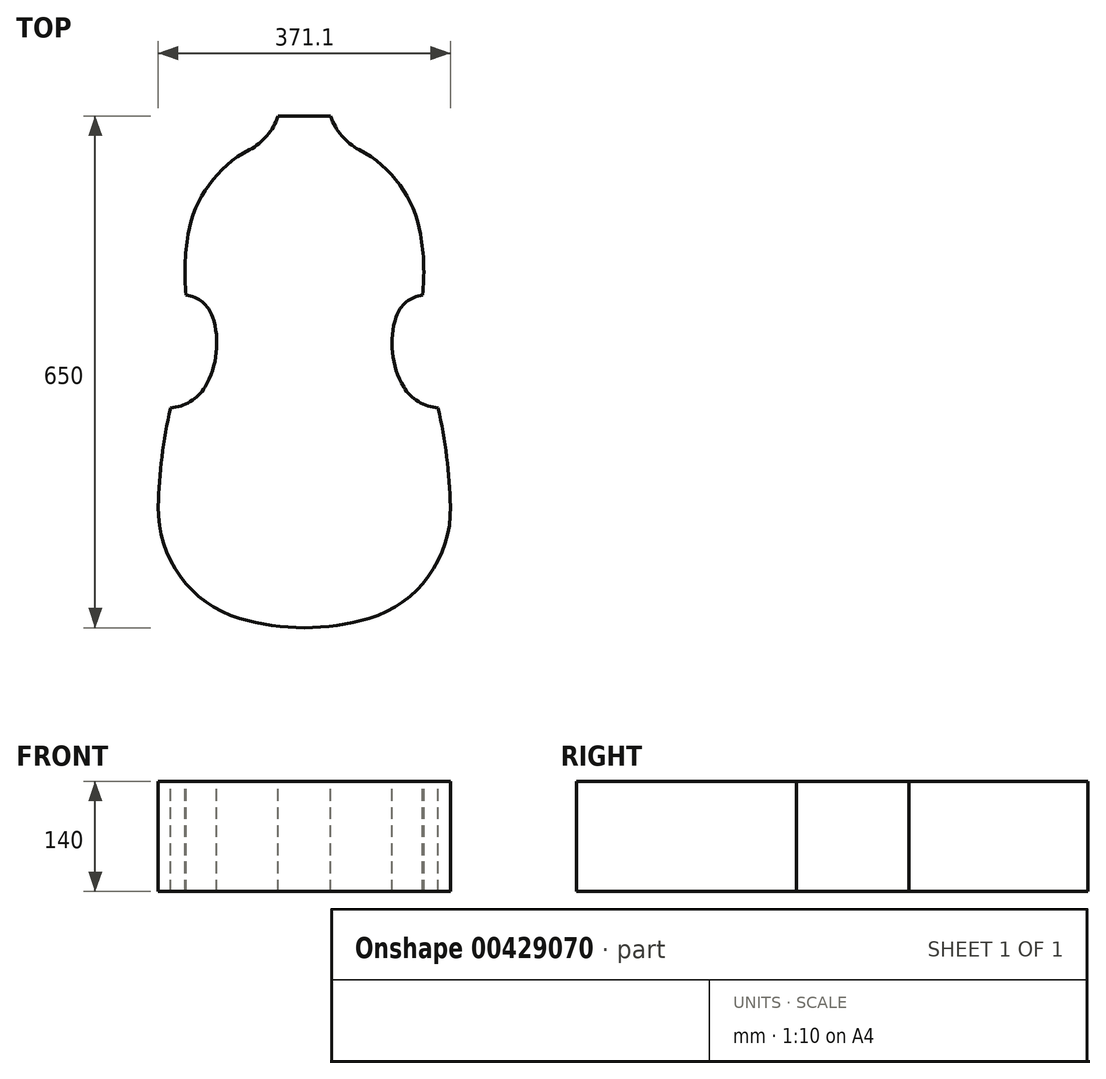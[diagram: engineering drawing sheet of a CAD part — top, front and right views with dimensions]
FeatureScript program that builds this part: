
annotation { "Feature Type Name" : "Feature", "Feature Type Description" : "" }
export const myFeature = defineFeature(function(context is Context, id is Id, definition is map)
    precondition{}
    {
        {
            var Q0;
            Q0=qCreatedBy(makeId("Top.planeOp"),FACE);
            var sketch = newSketch(context, id + "F0", { "sketchPlane" : qUnion([Q0])});
            skLineSegment(sketch, "E0", {"start": v(0, 0) * mm, "end": v(0, 680) * mm, "construction": true});
            skSolve(sketch);
        }
        {
            var Q0;
            Q0=qCreatedBy(makeId("Top.planeOp"),FACE);
            var sketch = newSketch(context, id + "F1", { "sketchPlane" : qUnion([Q0])});
            skLineSegment(sketch, "E1", {"start": v(0, 680) * mm, "end": v(0, 340) * mm});
            skLineSegment(sketch, "E2", {"start": v(0, 340) * mm, "end": v(0, 0) * mm});
            skLineSegment(sketch, "E3", {"start": v(0, 0) * mm, "end": v(0, -340) * mm});
            skSolve(sketch);
        }
        {
            var Q0;
            Q0=qCreatedBy(makeId("Top.planeOp"),FACE);
            var sketch = newSketch(context, id + "F2", { "sketchPlane" : qUnion([Q0])});
            skLineSegment(sketch, "E4", {"start": v(0, 0) * mm, "end": v(0, 68) * mm, "construction": true});
            skSolve(sketch);
        }
        {
            var Q0;
            Q0=qCreatedBy(makeId("Top.planeOp"),FACE);
            var sketch = newSketch(context, id + "F3", { "sketchPlane" : qUnion([Q0])});
            skLineSegment(sketch, "E5", {"start": v(0, 0) * mm, "end": v(0, 650) * mm, "construction": true});
            skPoint(sketch, "E6.endSnap0", {"position": v(0, 325) * mm});
            skLineSegment(sketch, "E7", {"start": v(0, 650) * mm, "end": v(377.25, 650) * mm, "construction": true});
            skSolve(sketch);
        }
        {
            var Q0;
            Q0=qCreatedBy(makeId("Top.planeOp"),FACE);
            var sketch = newSketch(context, id + "F4", { "sketchPlane" : qUnion([Q0])});
            skLineSegment(sketch, "E8", {"start": v(0, 650) * mm, "end": v(0, 577.78) * mm, "construction": true});
            skLineSegment(sketch, "E9", {"start": v(0, 577.78) * mm, "end": v(0, 505.56) * mm, "construction": true});
            skLineSegment(sketch, "E10", {"start": v(0, 505.56) * mm, "end": v(0, 433.33) * mm, "construction": true});
            skLineSegment(sketch, "E11", {"start": v(0, 433.33) * mm, "end": v(0, 361.11) * mm, "construction": true});
            skLineSegment(sketch, "E12", {"start": v(0, 361.11) * mm, "end": v(0, 288.89) * mm, "construction": true});
            skLineSegment(sketch, "E13", {"start": v(0, 288.89) * mm, "end": v(0, 216.67) * mm, "construction": true});
            skLineSegment(sketch, "E14", {"start": v(0, 216.67) * mm, "end": v(0, 144.44) * mm, "construction": true});
            skLineSegment(sketch, "E15", {"start": v(0, 144.44) * mm, "end": v(0, 72.22) * mm, "construction": true});
            skLineSegment(sketch, "E16", {"start": v(0, 72.22) * mm, "end": v(0, 0) * mm, "construction": true});
            skLineSegment(sketch, "E17", {"start": v(0, 0) * mm, "end": v(0, -72.22) * mm, "construction": true});
            skLineSegment(sketch, "E18", {"start": v(0, -72.22) * mm, "end": v(0, -144.44) * mm, "construction": true});
            skLineSegment(sketch, "E19", {"start": v(0, -144.44) * mm, "end": v(0, -216.67) * mm, "construction": true});
            skLineSegment(sketch, "E20", {"start": v(0, -216.67) * mm, "end": v(0, -288.89) * mm, "construction": true});
            skLineSegment(sketch, "E21", {"start": v(-33.5, -288.89) * mm, "end": v(33.5, -288.89) * mm, "construction": true});
            skLineSegment(sketch, "E22", {"start": v(-33.5, 361.11) * mm, "end": v(33.5, 361.11) * mm, "construction": true});
            skLineSegment(sketch, "E23", {"start": v(-577.47, 650) * mm, "end": v(577.47, 650) * mm, "construction": true});
            skLineSegment(sketch, "E24", {"start": v(-580.77, 0) * mm, "end": v(580.77, 0) * mm, "construction": true});
            skLineSegment(sketch, "E25", {"start": v(-583.98, 72.22) * mm, "end": v(583.98, 72.22) * mm, "construction": true});
            skSolve(sketch);
        }
        {
            var Q0;
            Q0=qCreatedBy(makeId("Top.planeOp"),FACE);
            var sketch = newSketch(context, id + "F5", { "sketchPlane" : qUnion([Q0])});
            skCircle(sketch, "E26", {"center": v(0, 0) * mm, "radius": 302.86 * mm});
            skCircle(sketch, "E27", {"center": v(262.29, -151.43) * mm, "radius": 462.53 * mm});
            skLineSegment(sketch, "E28", {"start": v(0, 0) * mm, "end": v(0, -302.86) * mm, "construction": true});
            skLineSegment(sketch, "E29", {"start": v(0, -302.86) * mm, "end": v(262.29, -151.43) * mm, "construction": true});
            skLineSegment(sketch, "E30", {"start": v(262.29, -151.43) * mm, "end": v(0, 0) * mm, "construction": true});
            skCircle(sketch, "E31", {"center": v(-48.7, -143.38) * mm, "radius": 151.43 * mm});
            skArc(sketch, "E32", {"start": v(0, -151.43) * mm, "mid": v(-32.38, -147.93) * mm, "end": v(-63.27, -137.58) * mm});
            skSolve(sketch);
        }
        {
            var Q0;
            Q0=qCreatedBy(makeId("Top.planeOp"),FACE);
            var sketch = newSketch(context, id + "F6", { "sketchPlane" : qUnion([Q0])});
            skLineSegment(sketch, "E33", {"start": v(651.57, 0) * mm, "end": v(651.57, 650) * mm, "construction": true});
            skLineSegment(sketch, "E34", {"start": v(651.57, 650) * mm, "end": v(756.75, 650) * mm, "construction": true});
            skLineSegment(sketch, "E35", {"start": v(756.75, 650) * mm, "end": v(756.75, 557.14) * mm, "construction": true});
            skLineSegment(sketch, "E36", {"start": v(756.75, 557.14) * mm, "end": v(756.75, 464.29) * mm, "construction": true});
            skLineSegment(sketch, "E37", {"start": v(756.75, 464.29) * mm, "end": v(756.75, 371.43) * mm, "construction": true});
            skLineSegment(sketch, "E38", {"start": v(756.75, 371.43) * mm, "end": v(756.75, 278.57) * mm, "construction": true});
            skLineSegment(sketch, "E39", {"start": v(756.75, 278.57) * mm, "end": v(756.75, 185.71) * mm, "construction": true});
            skLineSegment(sketch, "E40", {"start": v(756.75, 185.71) * mm, "end": v(756.75, 92.86) * mm, "construction": true});
            skLineSegment(sketch, "E41", {"start": v(756.75, 92.86) * mm, "end": v(756.75, 0) * mm, "construction": true});
            skLineSegment(sketch, "E42", {"start": v(756.75, 0) * mm, "end": v(651.57, 0) * mm, "construction": true});
            skLineSegment(sketch, "E43", {"start": v(-464.29, -151.43) * mm, "end": v(-464.29, 498.57) * mm, "construction": true});
            skLineSegment(sketch, "E44", {"start": v(-464.29, -151.43) * mm, "end": v(-371.43, -151.43) * mm, "construction": true});
            skLineSegment(sketch, "E45", {"start": v(-371.43, -151.43) * mm, "end": v(-278.57, -151.43) * mm, "construction": true});
            skLineSegment(sketch, "E46", {"start": v(-278.57, -151.43) * mm, "end": v(-185.71, -151.43) * mm, "construction": true});
            skLineSegment(sketch, "E47", {"start": v(-185.71, -151.43) * mm, "end": v(-92.86, -151.43) * mm, "construction": true});
            skLineSegment(sketch, "E48", {"start": v(-92.86, -151.43) * mm, "end": v(0, -151.43) * mm, "construction": true});
            skArc(sketch, "E49", {"start": v(-74.73, -279.05) * mm, "mid": v(122.25, -261.75) * mm, "end": v(261.95, -121.8) * mm});
            skArc(sketch, "E50", {"start": v(-464.29, 498.57) * mm, "mid": v(56.93, 236.94) * mm, "end": v(158.56, -337.34) * mm});
            skCircle(sketch, "E51", {"center": v(41.1, -138.47) * mm, "radius": 144.44 * mm});
            skLineSegment(sketch, "E52", {"start": v(41.1, -138.47) * mm, "end": v(41.1, -66.25) * mm, "construction": true});
            skLineSegment(sketch, "E53", {"start": v(41.1, -66.25) * mm, "end": v(41.1, 5.97) * mm, "construction": true});
            skSolve(sketch);
        }
        {
            var Q0;
            Q0=qCreatedBy(makeId("Top.planeOp"),FACE);
            var sketch = newSketch(context, id + "F7", { "sketchPlane" : qUnion([Q0])});
            skLineSegment(sketch, "E54", {"start": v(-464.29, -151.43) * mm, "end": v(-397.96, -88.53) * mm, "construction": true});
            skLineSegment(sketch, "E55", {"start": v(-397.96, -88.53) * mm, "end": v(-331.63, -25.63) * mm, "construction": true});
            skLineSegment(sketch, "E56", {"start": v(-331.63, -25.63) * mm, "end": v(-265.3, 37.28) * mm, "construction": true});
            skLineSegment(sketch, "E57", {"start": v(-265.3, 37.28) * mm, "end": v(-198.98, 100.18) * mm, "construction": true});
            skLineSegment(sketch, "E58", {"start": v(-198.98, 100.18) * mm, "end": v(-132.65, 163.08) * mm, "construction": true});
            skLineSegment(sketch, "E59", {"start": v(-132.65, 163.08) * mm, "end": v(-66.33, 225.99) * mm, "construction": true});
            skLineSegment(sketch, "E60", {"start": v(-66.33, 225.99) * mm, "end": v(0, 288.89) * mm, "construction": true});
            skCircle(sketch, "E61", {"center": v(-132.65, 163.08) * mm, "radius": 284.37 * mm});
            skLineSegment(sketch, "E62", {"start": v(-464.29, 498.57) * mm, "end": v(-464.29, 417.32) * mm, "construction": true});
            skLineSegment(sketch, "E63", {"start": v(-464.29, 417.32) * mm, "end": v(-464.29, 336.07) * mm, "construction": true});
            skLineSegment(sketch, "E64", {"start": v(-464.29, 336.07) * mm, "end": v(-464.29, 254.82) * mm, "construction": true});
            skLineSegment(sketch, "E65", {"start": v(-464.29, 254.82) * mm, "end": v(-464.29, 173.57) * mm, "construction": true});
            skLineSegment(sketch, "E66", {"start": v(-464.29, 173.57) * mm, "end": v(-464.29, 92.32) * mm, "construction": true});
            skLineSegment(sketch, "E67", {"start": v(-464.29, 92.32) * mm, "end": v(-464.29, 11.07) * mm, "construction": true});
            skLineSegment(sketch, "E68", {"start": v(-464.29, 11.07) * mm, "end": v(-464.29, -70.18) * mm, "construction": true});
            skLineSegment(sketch, "E69", {"start": v(-464.29, -70.18) * mm, "end": v(-464.29, -151.43) * mm, "construction": true});
            skCircle(sketch, "E70", {"center": v(-464.29, 132.94) * mm, "radius": 284.37 * mm, "construction": true});
            skPoint(sketch, "E70.centerSnap0", {"position": v(-464.29, 214.2) * mm});
            skLineSegment(sketch, "E71", {"start": v(-180.27, 325) * mm, "end": v(173.93, 325) * mm, "construction": true});
            skCircle(sketch, "E72", {"center": v(0, 185.71) * mm, "radius": 149.8 * mm});
            skCircle(sketch, "E73", {"center": v(104.63, 384.58) * mm, "radius": 74.9 * mm});
            skLineSegment(sketch, "E74", {"start": v(756.75, 185.71) * mm, "end": v(-927.16, 185.71) * mm});
            skLineSegment(sketch, "E75", {"start": v(-132.65, 163.08) * mm, "end": v(0, 185.71) * mm, "construction": true});
            skLineSegment(sketch, "E76", {"start": v(0, 185.71) * mm, "end": v(147.67, 210.9) * mm, "construction": true});
            skLineSegment(sketch, "E77", {"start": v(0, 185.71) * mm, "end": v(34.88, 252) * mm, "construction": true});
            skLineSegment(sketch, "E78", {"start": v(34.88, 252) * mm, "end": v(69.76, 318.29) * mm, "construction": true});
            skLineSegment(sketch, "E79", {"start": v(69.76, 318.29) * mm, "end": v(104.63, 384.58) * mm, "construction": true});
            skSolve(sketch);
        }
        {
            var Q0;
            Q0=qCreatedBy(makeId("Top.planeOp"),FACE);
            var sketch = newSketch(context, id + "F8", { "sketchPlane" : qUnion([Q0])});
            skLineSegment(sketch, "E80", {"start": v(0, 0) * mm, "end": v(0, -57.78) * mm, "construction": true});
            skLineSegment(sketch, "E81", {"start": v(0, -57.78) * mm, "end": v(0, -115.56) * mm, "construction": true});
            skLineSegment(sketch, "E82", {"start": v(0, -115.56) * mm, "end": v(0, -173.33) * mm, "construction": true});
            skLineSegment(sketch, "E83", {"start": v(0, -173.33) * mm, "end": v(0, -231.11) * mm, "construction": true});
            skLineSegment(sketch, "E84", {"start": v(0, -231.11) * mm, "end": v(0, -288.89) * mm, "construction": true});
            skCircle(sketch, "E85", {"center": v(-219.54, 72.22) * mm, "radius": 108.33 * mm});
            skArc(sketch, "E86", {"start": v(0, -231.11) * mm, "mid": v(-187.22, -135.5) * mm, "end": v(-219.54, 72.22) * mm, "construction": true});
            skLineSegment(sketch, "E87", {"start": v(0, 0) * mm, "end": v(0, 108.33) * mm, "construction": true});
            skLineSegment(sketch, "E88", {"start": v(0, 108.33) * mm, "end": v(0, 216.67) * mm, "construction": true});
            skLineSegment(sketch, "E89", {"start": v(0, 216.67) * mm, "end": v(0, 325) * mm, "construction": true});
            skLineSegment(sketch, "E90", {"start": v(0, 325) * mm, "end": v(0, 433.33) * mm, "construction": true});
            skLineSegment(sketch, "E91", {"start": v(0, 433.33) * mm, "end": v(0, 541.67) * mm, "construction": true});
            skLineSegment(sketch, "E92", {"start": v(0, 541.67) * mm, "end": v(0, 650) * mm, "construction": true});
            skLineSegment(sketch, "E93", {"start": v(-219.54, 72.22) * mm, "end": v(-327.87, 72.22) * mm, "construction": true});
            skLineSegment(sketch, "E94", {"start": v(609.32, 650) * mm, "end": v(609.32, 568.75) * mm});
            skLineSegment(sketch, "E95", {"start": v(609.32, 568.75) * mm, "end": v(609.32, 487.5) * mm});
            skLineSegment(sketch, "E96", {"start": v(609.32, 487.5) * mm, "end": v(609.32, 406.25) * mm});
            skLineSegment(sketch, "E97", {"start": v(609.32, 406.25) * mm, "end": v(609.32, 325) * mm});
            skLineSegment(sketch, "E98", {"start": v(609.32, 325) * mm, "end": v(609.32, 243.75) * mm});
            skLineSegment(sketch, "E99", {"start": v(609.32, 243.75) * mm, "end": v(609.32, 162.5) * mm});
            skLineSegment(sketch, "E100", {"start": v(609.32, 162.5) * mm, "end": v(609.32, 81.25) * mm});
            skLineSegment(sketch, "E101", {"start": v(609.32, 81.25) * mm, "end": v(609.32, 0) * mm});
            skCircle(sketch, "E102", {"center": v(609.32, 40.62) * mm, "radius": 40.62 * mm});
            skCircle(sketch, "E103", {"center": v(-172.93, 44.62) * mm, "radius": 54.17 * mm});
            skLineSegment(sketch, "E104", {"start": v(-219.54, 72.22) * mm, "end": v(-155.22, 93.38) * mm, "construction": true});
            skCircle(sketch, "E105", {"center": v(-155.22, 93.38) * mm, "radius": 40.62 * mm});
            skLineSegment(sketch, "E106", {"start": v(-219.54, 72.22) * mm, "end": v(0, -57.78) * mm, "construction": true});
            skLineSegment(sketch, "E107", {"start": v(-155.22, 93.38) * mm, "end": v(0, 144.44) * mm, "construction": true});
            skArc(sketch, "E108", {"start": v(0, -231.11) * mm, "mid": v(187.22, -135.5) * mm, "end": v(219.54, 72.22) * mm, "construction": true});
            skLineSegment(sketch, "E109", {"start": v(0, 144.44) * mm, "end": v(219.54, 72.22) * mm, "construction": true});
            skLineSegment(sketch, "E110", {"start": v(0, -57.78) * mm, "end": v(219.54, 72.22) * mm, "construction": true});
            skCircle(sketch, "E111", {"center": v(219.54, 72.22) * mm, "radius": 108.33 * mm});
            skLineSegment(sketch, "E112", {"start": v(219.54, 72.22) * mm, "end": v(327.87, 72.22) * mm, "construction": true});
            skCircle(sketch, "E113", {"center": v(155.22, 93.38) * mm, "radius": 40.62 * mm});
            skCircle(sketch, "E114", {"center": v(172.93, 44.62) * mm, "radius": 54.17 * mm});
            skSolve(sketch);
        }
        {
            var Q0;
            Q0=qCreatedBy(makeId("Top.planeOp"),FACE);
            var sketch = newSketch(context, id + "F9", { "sketchPlane" : qUnion([Q0])});
            skPoint(sketch, "E115.orphan", {"position": v(-464.29, 498.57) * mm});
            skLineSegment(sketch, "E116", {"start": v(33.5, 361.11) * mm, "end": v(0, 361.11) * mm});
            skLineSegment(sketch, "E117", {"start": v(0, 361.11) * mm, "end": v(0, -288.89) * mm});
            skArc(sketch, "E118.0", {"start": v(33.5, 361.11) * mm, "mid": v(47.47, 336.18) * mm, "end": v(69.76, 318.29) * mm});
            skArc(sketch, "E119.0", {"start": v(147.67, 210.9) * mm, "mid": v(121.25, 273.7) * mm, "end": v(69.76, 318.29) * mm});
            skArc(sketch, "E120.0", {"start": v(150.2, 133.7) * mm, "mid": v(129.4, 124.75) * mm, "end": v(116.63, 106.08) * mm});
            skArc(sketch, "E121.0", {"start": v(116.63, 106.08) * mm, "mid": v(111.84, 60.5) * mm, "end": v(126.32, 17.02) * mm});
            skArc(sketch, "E122.0", {"start": v(82.2, -276.95) * mm, "mid": v(157.96, -223.37) * mm, "end": v(185.5, -134.77) * mm});
            skArc(sketch, "E123.0", {"start": v(0, -288.89) * mm, "mid": v(41.54, -285.89) * mm, "end": v(82.2, -276.95) * mm});
            skPoint(sketch, "E124.orphan", {"position": v(-74.73, -279.05) * mm});
            skPoint(sketch, "E125.orphan", {"position": v(158.56, -337.34) * mm});
            skPoint(sketch, "E126.orphan", {"position": v(261.95, -121.8) * mm});
            skArc(sketch, "E127.trimOffspring", {"start": v(170.02, -9.47) * mm, "mid": v(180.81, -71.74) * mm, "end": v(185.5, -134.77) * mm});
            skArc(sketch, "E128.trimOffspring", {"start": v(150.2, 133.7) * mm, "mid": v(151.57, 172.39) * mm, "end": v(147.67, 210.9) * mm});
            skArc(sketch, "E129.trimOffspring", {"start": v(126.32, 17.02) * mm, "mid": v(144.85, -1.7) * mm, "end": v(170.02, -9.47) * mm});
            skSolve(sketch);
        }
        {
            var Q0;
            Q0 = qSketchRegion(id + "F9", true);
            extrude(context, id + "F10", {"entities" : qUnion([Q0]), "oppositeDirection" : true, "depth" : 140 * mm});
        }
        {
            var Q0;
            Q0=makeQuery(id+"F10.opExtrude","SWEPT_BODY",BODY,{"disambiguationData":[OSD([sQuery(id+"F9.wireOp",EDGE,"E116"),sQuery(id+"F9.wireOp",EDGE,"E117"),sQuery(id+"F9.wireOp",EDGE,"E118.0"),sQuery(id+"F9.wireOp",EDGE,"E119.0"),sQuery(id+"F9.wireOp",EDGE,"E120.0"),sQuery(id+"F9.wireOp",EDGE,"E121.0"),sQuery(id+"F9.wireOp",EDGE,"E122.0"),sQuery(id+"F9.wireOp",EDGE,"E123.0"),sQuery(id+"F9.wireOp",EDGE,"E127.trimOffspring"),sQuery(id+"F9.wireOp",EDGE,"E128.trimOffspring"),sQuery(id+"F9.wireOp",EDGE,"E129.trimOffspring")])]});
            var Q1;
            Q1=makeQuery(id+"F10.opExtrude","SWEPT_FACE",FACE,{"disambiguationData":[OSD([sQuery(id+"F9.wireOp",EDGE,"E117")])]});
            mirror(context, id + "F11", {"operationType" : NewBodyOperationType.ADD, "entities" : qUnion([Q0]), "mirrorPlane" : qUnion([Q1])});
        }
    });
